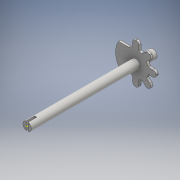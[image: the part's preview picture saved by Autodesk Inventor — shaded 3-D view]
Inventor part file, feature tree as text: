
AUTODESK INVENTOR PART (.ipt)
format: ipt  version: 2016 (Build 200138000, 138)  size: 178,688 bytes
history: native  units: mm
features: sketch x5, extrude x4, fillet x1
ambient origin geometry x8: Origin, YZ Plane, XZ Plane, XY Plane, X Axis, Y Axis, Z Axis, Center Point
bodies: Solid1 (feature_tree)
feature tree (10):
  sketch  "Sketch1"  dims[d0=4.0mm d1=51.0mm d2=0.0mm]
  extrude  "Extrusion1"  Depth=51.0mm TaperAngle=0.0deg
  extrude  "Extrusion2"  Depth=4.0mm
  extrude  "Extrusion3"  Depth=4.0mm
  fillet  "Fillet1"  Radius=5.0mm
  extrude  "Extrusion4"  Depth=1.4mm
  sketch  "Sketch2"  dims[d3=1.0mm d4=4.0mm]
  sketch  "Sketch3"  dims[d5=4.0mm d6=0.0mm d28=5.0mm d29=5.0mm]
  sketch  "Sketch4"  dims[d30=1.0mm d31=0.0mm d32=1.4mm]
  sketch  "Sketch5"  dims[d33=4.0mm d34=7.0mm d35=0.0mm]
